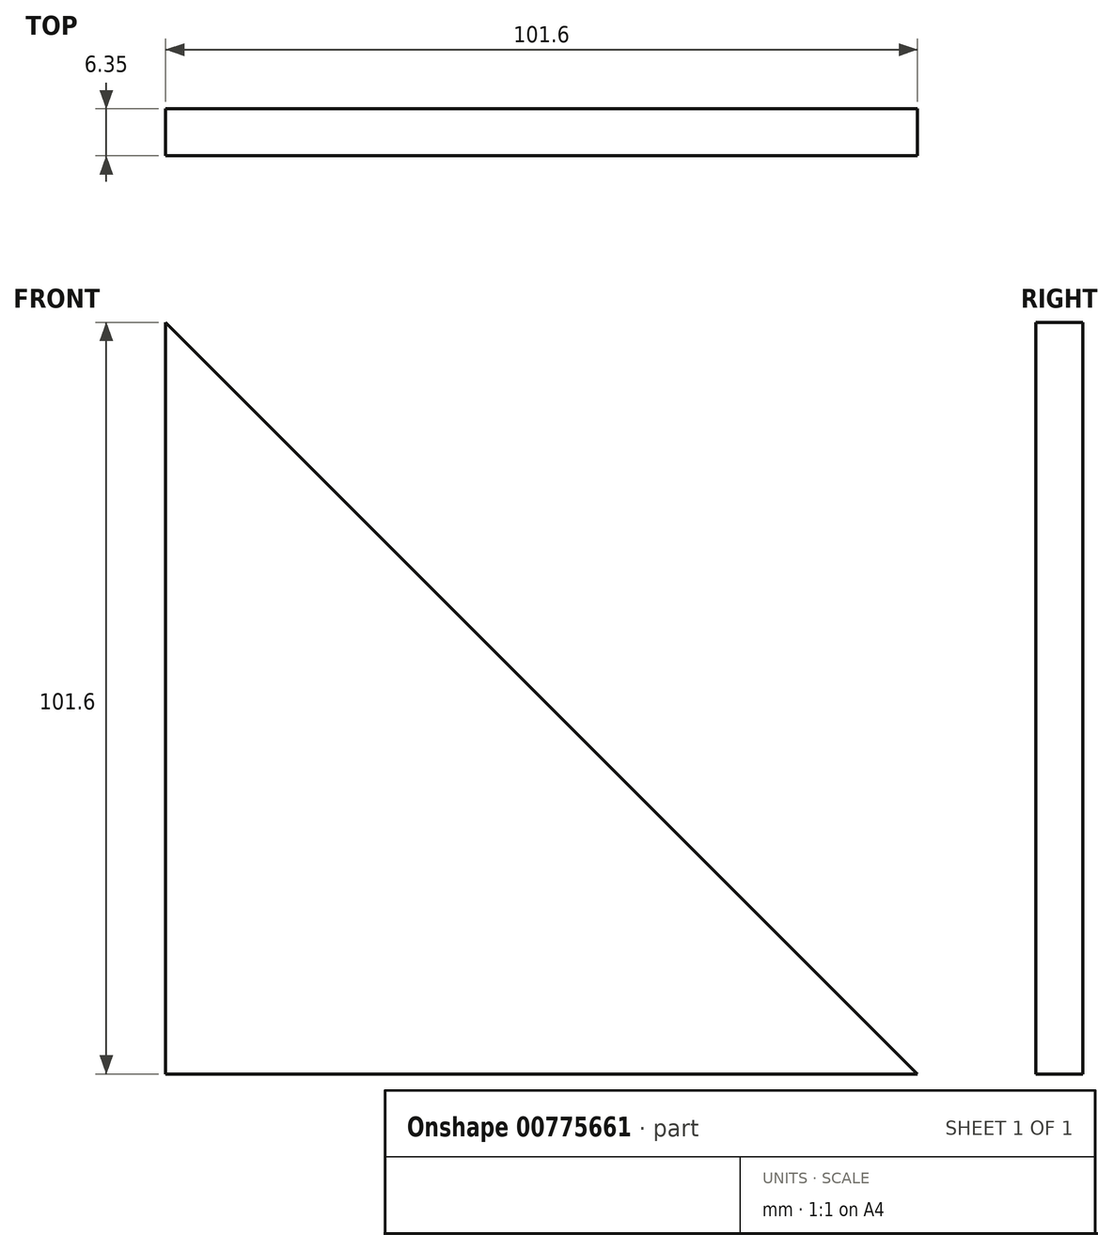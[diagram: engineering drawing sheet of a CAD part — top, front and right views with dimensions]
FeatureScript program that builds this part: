
annotation { "Feature Type Name" : "Feature", "Feature Type Description" : "" }
export const myFeature = defineFeature(function(context is Context, id is Id, definition is map)
    precondition{}
    {
        {
            var Q0;
            Q0=qCreatedBy(makeId("Front.planeOp"),FACE);
            var sketch = newSketch(context, id + "F0", { "sketchPlane" : qUnion([Q0])});
            skLineSegment(sketch, "E0", {"start": v(0, 0) * mm, "end": v(0, 101.6) * mm});
            skLineSegment(sketch, "E1", {"start": v(0, 101.6) * mm, "end": v(101.6, 0) * mm});
            skLineSegment(sketch, "E2", {"start": v(101.6, 0) * mm, "end": v(0, 0) * mm});
            skSolve(sketch);
        }
        {
            var Q0;
            Q0=makeQuery(id+"F0.imprint","IMPRINT",FACE,{"disambiguationData":[TD([[makeQuery(id+"F0.imprint","IMPRINT",EDGE,{"derivedFrom":sQuery(id+"F0.wireOp",EDGE,"E0")}),-1.0]])]});
            var sketch = newSketch(context, id + "F1", { "sketchPlane" : qUnion([Q0])});
            skSolve(sketch);
        }
        {
            var Q0;
            Q0 = qSketchRegion(id + "F1", true);
            var Q1;
            Q1=makeQuery(id+"F1.imprint","IMPRINT",FACE,{"disambiguationData":[TD([[makeQuery(id+"F1.imprint","IMPRINT",EDGE,{"derivedFrom":makeQuery(id+"F0.imprint","IMPRINT",EDGE,{"derivedFrom":sQuery(id+"F0.wireOp",EDGE,"E0")})}),-1.0]])]});
            extrude(context, id + "F2", {"entities" : qUnion([Q0, Q1]), "depth" : 6.35 * mm, "offsetDistance" : 25 * mm});
        }
    });
